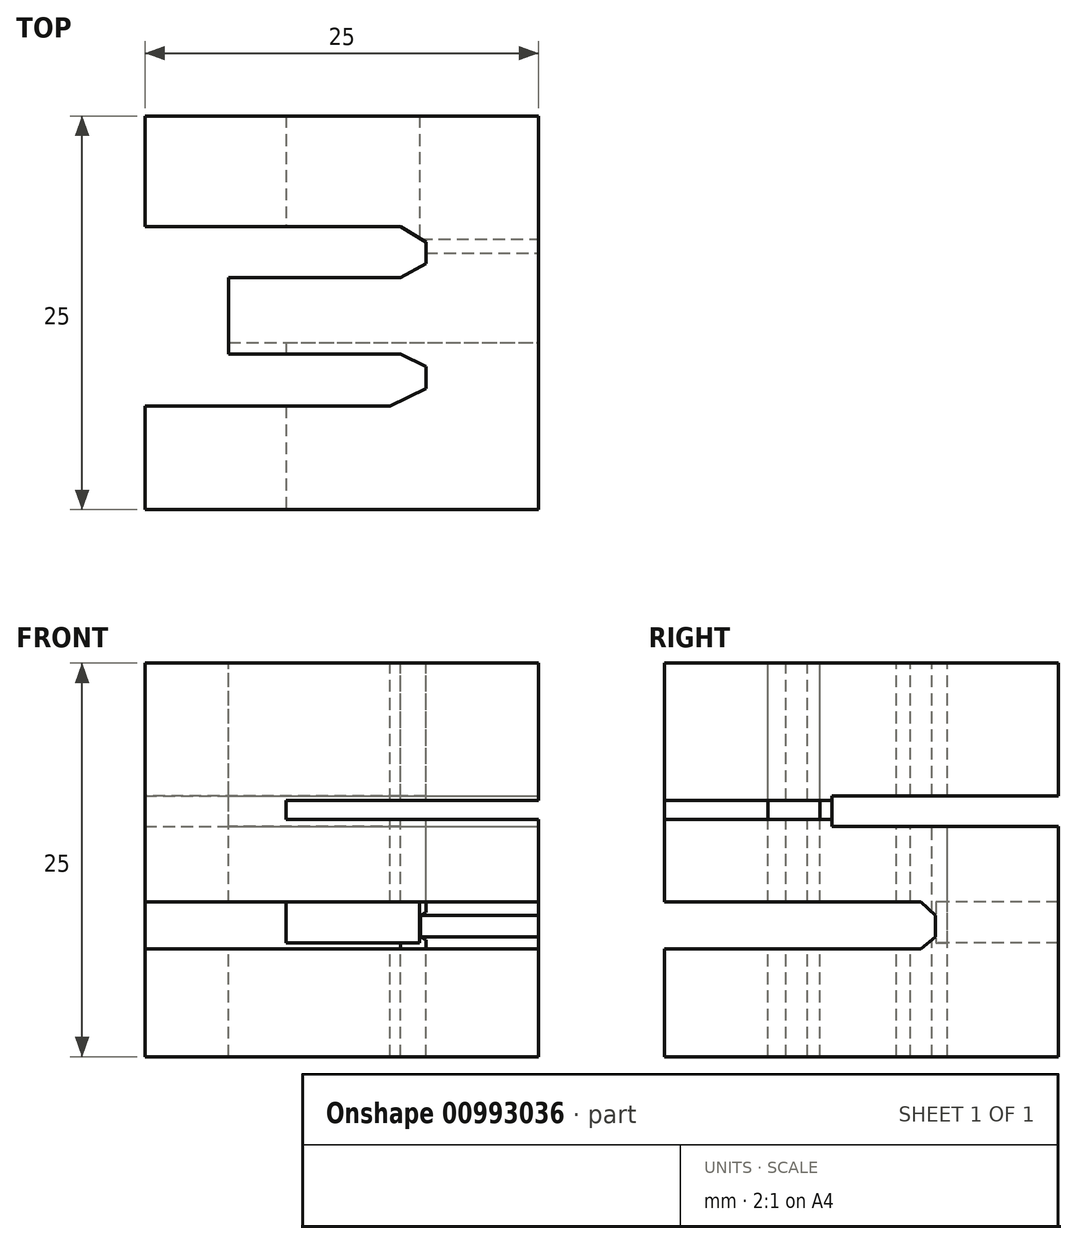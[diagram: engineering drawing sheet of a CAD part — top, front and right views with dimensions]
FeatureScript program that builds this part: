
annotation { "Feature Type Name" : "Feature", "Feature Type Description" : "" }
export const myFeature = defineFeature(function(context is Context, id is Id, definition is map)
    precondition{}
    {
        {
            var Q0;
            Q0=qCreatedBy(makeId("Top.planeOp"),FACE);
            var sketch = newSketch(context, id + "F0", { "sketchPlane" : qUnion([Q0])});
            skLineSegment(sketch, "E0.bottom", {"start": v(12.5, 12.5) * mm, "end": v(-12.5, 12.5) * mm});
            skLineSegment(sketch, "E0.top", {"start": v(12.5, -12.5) * mm, "end": v(-12.5, -12.5) * mm});
            skLineSegment(sketch, "E0.left", {"start": v(12.5, 12.5) * mm, "end": v(12.5, -12.5) * mm});
            skLineSegment(sketch, "E0.right", {"start": v(-12.5, 12.5) * mm, "end": v(-12.5, -12.5) * mm});
            skPoint(sketch, "E0.middle", {"position": v(0, 0) * mm});
            skSolve(sketch);
        }
        {
            var Q0;
            Q0=makeQuery(id+"F0.imprint","IMPRINT",FACE,{"disambiguationData":[TD([[makeQuery(id+"F0.imprint","IMPRINT",EDGE,{"derivedFrom":sQuery(id+"F0.wireOp",EDGE,"E0.bottom")}),1.0]])]});
            extrude(context, id + "F1", {"entities" : qUnion([Q0]), "depth" : 25 * mm, "offsetDistance" : 25 * mm});
        }
        {
            var Q0;
            Q0=makeQuery(id+"F1.opExtrude","SWEPT_FACE",FACE,{"disambiguationData":[OSD([sQuery(id+"F0.wireOp",EDGE,"E0.top")])]});
            var sketch = newSketch(context, id + "F2", { "sketchPlane" : qUnion([Q0])});
            skLineSegment(sketch, "E1", {"start": v(12.5, 25) * mm, "end": v(-12.5, 25) * mm});
            skLineSegment(sketch, "E2", {"start": v(-12.5, 25) * mm, "end": v(-12.5, 0) * mm});
            skLineSegment(sketch, "E3", {"start": v(-12.5, 0) * mm, "end": v(12.5, 0) * mm});
            skLineSegment(sketch, "E4", {"start": v(12.5, 0) * mm, "end": v(12.5, 15.07) * mm});
            skLineSegment(sketch, "E5", {"start": v(12.5, 15.07) * mm, "end": v(-3.55, 15.07) * mm});
            skLineSegment(sketch, "E6", {"start": v(-3.55, 15.07) * mm, "end": v(-3.55, 16.28) * mm});
            skLineSegment(sketch, "E7", {"start": v(-3.55, 16.28) * mm, "end": v(12.5, 16.28) * mm});
            skLineSegment(sketch, "E8", {"start": v(12.5, 16.28) * mm, "end": v(12.5, 25) * mm});
            skLineSegment(sketch, "E9", {"start": v(-3.55, 9.82) * mm, "end": v(-3.55, 7.23) * mm});
            skLineSegment(sketch, "E10", {"start": v(-3.55, 7.23) * mm, "end": v(4.94, 7.23) * mm});
            skLineSegment(sketch, "E11", {"start": v(4.94, 7.23) * mm, "end": v(4.94, 9.82) * mm});
            skLineSegment(sketch, "E12", {"start": v(4.94, 9.82) * mm, "end": v(-3.55, 9.82) * mm});
            skSolve(sketch);
        }
        {
            var Q0;
            Q0=makeQuery(id+"F1.opExtrude","SWEPT_FACE",FACE,{"disambiguationData":[OSD([sQuery(id+"F0.wireOp",EDGE,"E0.left")])]});
            var sketch = newSketch(context, id + "F3", { "sketchPlane" : qUnion([Q0])});
            skLineSegment(sketch, "E13", {"start": v(12.5, 25) * mm, "end": v(-12.5, 25) * mm});
            skLineSegment(sketch, "E14", {"start": v(-12.5, 25) * mm, "end": v(-12.5, 9.82) * mm});
            skPoint(sketch, "E15", {"position": v(-12.5, 12.5) * mm});
            skLineSegment(sketch, "E16", {"start": v(-12.5, 9.82) * mm, "end": v(3.78, 9.82) * mm});
            skLineSegment(sketch, "E17", {"start": v(3.78, 9.82) * mm, "end": v(4.7, 8.97) * mm});
            skLineSegment(sketch, "E18", {"start": v(4.7, 8.97) * mm, "end": v(4.7, 7.6) * mm});
            skLineSegment(sketch, "E19", {"start": v(4.7, 7.6) * mm, "end": v(3.78, 6.85) * mm});
            skLineSegment(sketch, "E20", {"start": v(3.78, 6.85) * mm, "end": v(-12.5, 6.85) * mm});
            skLineSegment(sketch, "E21", {"start": v(-12.5, 6.85) * mm, "end": v(-12.5, 0) * mm});
            skLineSegment(sketch, "E22", {"start": v(-12.5, 0) * mm, "end": v(12.5, 0) * mm});
            skLineSegment(sketch, "E23", {"start": v(12.5, 0) * mm, "end": v(12.5, 14.63) * mm});
            skLineSegment(sketch, "E24", {"start": v(12.5, 14.63) * mm, "end": v(-1.88, 14.63) * mm});
            skLineSegment(sketch, "E25", {"start": v(-1.88, 14.63) * mm, "end": v(-1.88, 16.57) * mm});
            skLineSegment(sketch, "E26", {"start": v(-1.88, 16.57) * mm, "end": v(12.5, 16.57) * mm});
            skLineSegment(sketch, "E27", {"start": v(12.5, 16.57) * mm, "end": v(12.5, 25) * mm});
            skSolve(sketch);
        }
        {
            var Q0;
            Q0=makeQuery(id+"F1.opExtrude","CAP_FACE",FACE,{"disambiguationData":[OSD([sQuery(id+"F0.wireOp",EDGE,"E0.bottom"),sQuery(id+"F0.wireOp",EDGE,"E0.top"),sQuery(id+"F0.wireOp",EDGE,"E0.left"),sQuery(id+"F0.wireOp",EDGE,"E0.right")])],"isStart":false});
            var sketch = newSketch(context, id + "F4", { "sketchPlane" : qUnion([Q0])});
            skLineSegment(sketch, "E28", {"start": v(-12.5, 12.5) * mm, "end": v(12.5, 12.5) * mm});
            skLineSegment(sketch, "E29", {"start": v(12.5, 12.5) * mm, "end": v(12.5, -12.5) * mm});
            skLineSegment(sketch, "E30", {"start": v(12.5, -12.5) * mm, "end": v(-12.5, -12.5) * mm});
            skLineSegment(sketch, "E31", {"start": v(-12.5, -12.5) * mm, "end": v(-12.5, -5.94) * mm});
            skLineSegment(sketch, "E32", {"start": v(-12.5, -5.94) * mm, "end": v(3.08, -5.94) * mm});
            skLineSegment(sketch, "E33", {"start": v(3.08, -5.94) * mm, "end": v(5.34, -4.8) * mm});
            skLineSegment(sketch, "E34", {"start": v(5.34, -4.8) * mm, "end": v(5.34, -3.43) * mm});
            skLineSegment(sketch, "E35", {"start": v(5.34, -3.43) * mm, "end": v(3.73, -2.62) * mm});
            skLineSegment(sketch, "E36", {"start": v(3.73, -2.62) * mm, "end": v(-7.19, -2.62) * mm});
            skLineSegment(sketch, "E37", {"start": v(-7.19, -2.62) * mm, "end": v(-7.19, 2.23) * mm});
            skLineSegment(sketch, "E38", {"start": v(-7.19, 2.23) * mm, "end": v(3.73, 2.23) * mm});
            skLineSegment(sketch, "E39", {"start": v(3.73, 2.23) * mm, "end": v(5.34, 3.12) * mm});
            skLineSegment(sketch, "E40", {"start": v(5.34, 3.12) * mm, "end": v(5.34, 4.5) * mm});
            skLineSegment(sketch, "E41", {"start": v(5.34, 4.5) * mm, "end": v(3.73, 5.46) * mm});
            skLineSegment(sketch, "E42", {"start": v(3.73, 5.46) * mm, "end": v(-12.5, 5.46) * mm});
            skLineSegment(sketch, "E43", {"start": v(-12.5, 5.46) * mm, "end": v(-12.5, 12.5) * mm});
            skSolve(sketch);
        }
        {
            var Q0;
            Q0=makeQuery(id+"F4.imprint","IMPRINT",FACE,{"disambiguationData":[TD([[makeQuery(id+"F4.imprint","IMPRINT",EDGE,{"derivedFrom":sQuery(id+"F4.wireOp",EDGE,"E28")}),1.0]])]});
            extrude(context, id + "F5", {"entities" : qUnion([Q0]), "operationType" : NewBodyOperationType.INTERSECT, "oppositeDirection" : true, "depth" : 32.1 * mm, "offsetDistance" : 25 * mm});
        }
        {
            var Q0;
            Q0=makeQuery(id+"F3.imprint","IMPRINT",FACE,{"disambiguationData":[TD([[makeQuery(id+"F3.imprint","IMPRINT",EDGE,{"derivedFrom":sQuery(id+"F3.wireOp",EDGE,"E13")}),1.0]])]});
            extrude(context, id + "F6", {"entities" : qUnion([Q0]), "operationType" : NewBodyOperationType.INTERSECT, "oppositeDirection" : true, "depth" : 40.6 * mm, "offsetDistance" : 25 * mm});
        }
        {
            var Q0;
            Q0=makeQuery(id+"F2.imprint","IMPRINT",FACE,{"disambiguationData":[TD([[makeQuery(id+"F2.imprint","IMPRINT",EDGE,{"derivedFrom":sQuery(id+"F2.wireOp",EDGE,"E1")}),1.0]])]});
            extrude(context, id + "F7", {"entities" : qUnion([Q0]), "operationType" : NewBodyOperationType.INTERSECT, "oppositeDirection" : true, "depth" : 45.1 * mm, "offsetDistance" : 25 * mm});
        }
    });
